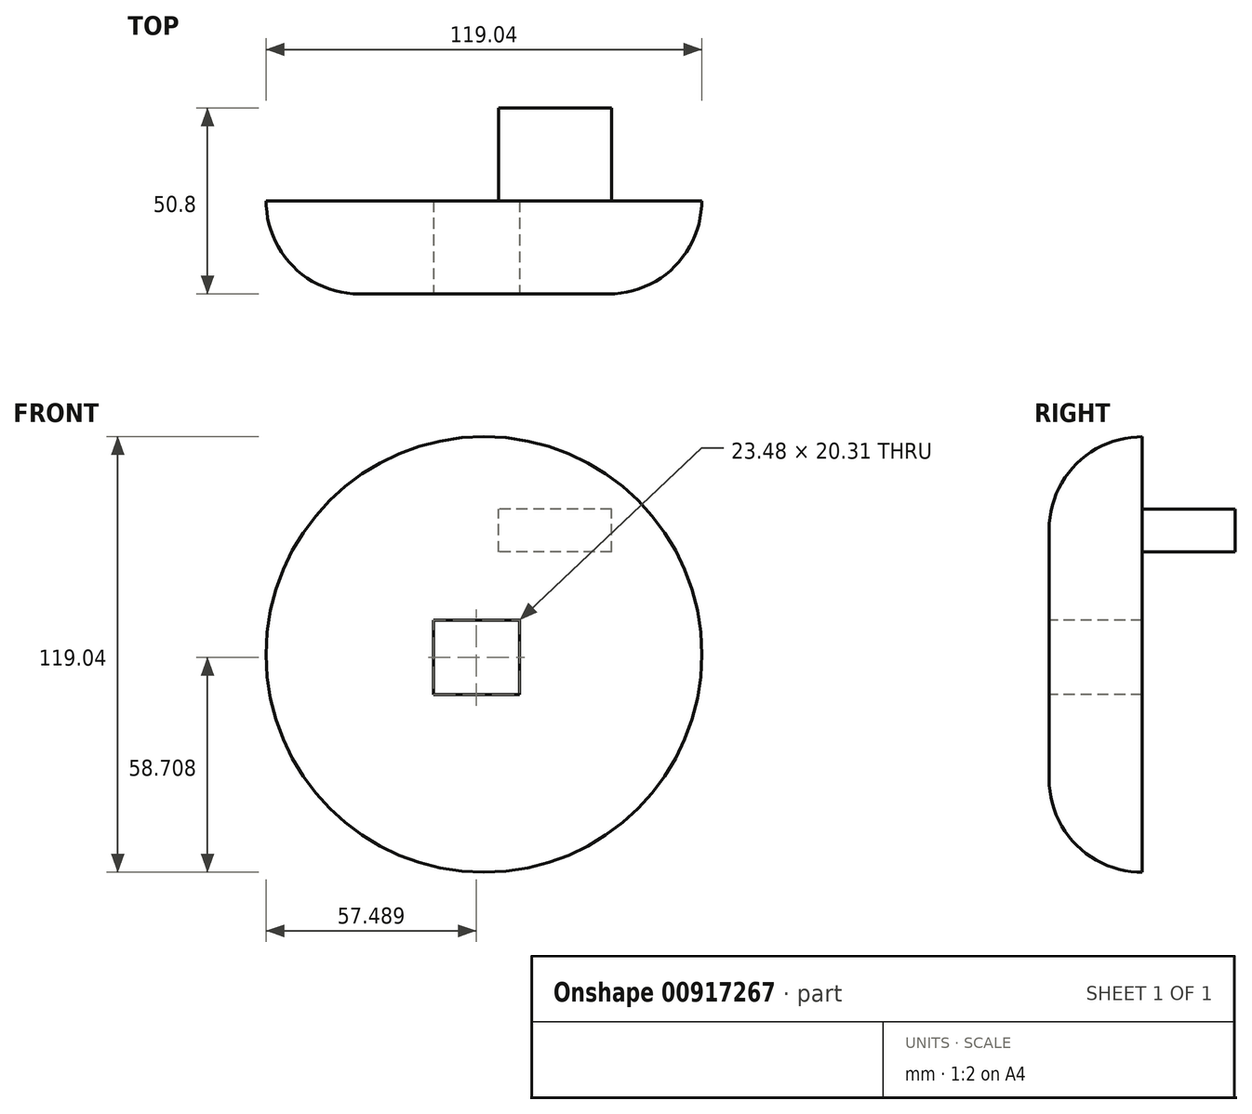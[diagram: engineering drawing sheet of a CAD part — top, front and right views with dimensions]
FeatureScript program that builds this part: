
annotation { "Feature Type Name" : "Feature", "Feature Type Description" : "" }
export const myFeature = defineFeature(function(context is Context, id is Id, definition is map)
    precondition{}
    {
        {
            var Q0;
            Q0=qCreatedBy(makeId("Front.planeOp"),FACE);
            var sketch = newSketch(context, id + "F0", { "sketchPlane" : qUnion([Q0])});
            skCircle(sketch, "E0", {"center": v(0, 0) * mm, "radius": 58.19 * mm});
            skSolve(sketch);
        }
        {
            var Q0;
            Q0 = qSketchRegion(id + "F0", true);
            extrude(context, id + "F1", {"entities" : qUnion([Q0]), "oppositeDirection" : true, "depth" : 25.4 * mm, "offsetDistance" : 25.4 * mm, "hasDraft" : true, "draftAngle" : 3 * degree});
        }
        {
            var Q0;
            Q0=makeQuery(id+"F1.opExtrude","CAP_FACE",FACE,{"disambiguationData":[OSD([sQuery(id+"F0.wireOp",EDGE,"E0")])],"isStart":true});
            var sketch = newSketch(context, id + "F2", { "sketchPlane" : qUnion([Q0])});
            skLineSegment(sketch, "E1.bottom", {"start": v(-13.77, 9.34) * mm, "end": v(9.7, 9.34) * mm});
            skLineSegment(sketch, "E1.top", {"start": v(-13.77, -10.97) * mm, "end": v(9.7, -10.97) * mm});
            skLineSegment(sketch, "E1.left", {"start": v(-13.77, 9.34) * mm, "end": v(-13.77, -10.97) * mm});
            skLineSegment(sketch, "E1.right", {"start": v(9.7, 9.34) * mm, "end": v(9.7, -10.97) * mm});
            skSolve(sketch);
        }
        {
            var Q0;
            Q0 = qSketchRegion(id + "F2", true);
            var Q1;
            Q1=makeQuery(id+"F1.opExtrude","CAP_FACE",FACE,{"disambiguationData":[OSD([sQuery(id+"F0.wireOp",EDGE,"E0")])],"isStart":false});
            extrude(context, id + "F3", {"entities" : qUnion([Q0]), "operationType" : NewBodyOperationType.REMOVE, "endBound" : BoundingType.UP_TO_SURFACE, "oppositeDirection" : true, "depth" : 83.06 * mm, "endBoundEntityFace" : qUnion([Q1]), "offsetDistance" : 25.4 * mm});
        }
        {
            var Q0;
            Q0=makeQuery(id+"F1.opExtrude","CAP_EDGE",EDGE,{"disambiguationData":[OSD([sQuery(id+"F0.wireOp",EDGE,"E0")])],"isStart":true});
            fillet(context, id + "F4", {"entities" : qUnion([Q0]), "radius" : 25.4 * mm, "tangentPropagation" : true, "allowEdgeOverflow" : false});
        }
        {
            var Q0;
            Q0=makeQuery(id+"F1.opExtrude","CAP_FACE",FACE,{"disambiguationData":[OSD([sQuery(id+"F0.wireOp",EDGE,"E0")])],"isStart":false});
            var sketch = newSketch(context, id + "F5", { "sketchPlane" : qUnion([Q0])});
            skLineSegment(sketch, "E2.bottom", {"start": v(-34.87, 28) * mm, "end": v(-3.96, 28) * mm});
            skLineSegment(sketch, "E2.top", {"start": v(-34.87, 39.75) * mm, "end": v(-3.96, 39.75) * mm});
            skLineSegment(sketch, "E2.left", {"start": v(-34.87, 28) * mm, "end": v(-34.87, 39.75) * mm});
            skLineSegment(sketch, "E2.right", {"start": v(-3.96, 28) * mm, "end": v(-3.96, 39.75) * mm});
            skSolve(sketch);
        }
        {
            var Q0;
            Q0 = qSketchRegion(id + "F5", true);
            extrude(context, id + "F6", {"entities" : qUnion([Q0]), "operationType" : NewBodyOperationType.ADD, "depth" : 25.4 * mm, "offsetDistance" : 25.4 * mm});
        }
    });
